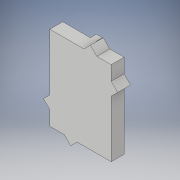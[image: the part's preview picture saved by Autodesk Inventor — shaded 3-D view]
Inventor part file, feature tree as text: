
AUTODESK INVENTOR PART (.ipt)
format: ipt  version: 2019 (Build 230136000, 136)  size: 216,576 bytes
history: native  units: mm
features: extrude x9, sketch x8
ambient origin geometry x8: Origin, YZ Plane, XZ Plane, XY Plane, X Axis, Y Axis, Z Axis, Center Point
bodies: Volumenkörper1 (feature_tree)
feature tree (17):
  sketch  "Skizze1"  dims[d0=50.5mm d1=35.5mm]
  extrude  "Extrusion1"  Depth=35.5mm
  extrude  "Extrusion2"  Depth=2.5mm TaperAngle=0.0deg
  extrude  "Extrusion3"  Depth=6.0mm
  extrude  "Extrusion4"  Depth=6.0mm
  extrude  "Extrusion5"  Depth=6.0mm TaperAngle=0.0deg
  extrude  "Extrusion8"  Depth=7.0mm
  extrude  "Extrusion9"  Depth=3.3mm
  extrude  "Extrusion10"  Depth=2.5mm TaperAngle=0.0deg
  extrude  "Extrusion11"  Depth=4.0mm
  sketch  "Skizze2"  dims[d2=2.5mm d3=2.5mm d4=0.0mm]
  sketch  "Skizze3"  dims[d5=6.0mm d6=0.0mm d7=3.0mm]
  sketch  "Skizze4"  dims[d8=77.5mm d9=0.0mm d11=6.0mm]
  sketch  "Skizze7"  dims[d12=6.0mm d13=0.0mm d15=6.0mm d16=0.0mm]
  sketch  "Skizze8"  dims[d26=7.0mm d27=7.0mm]
  sketch  "Skizze9"  dims[d28=3.3mm d29=3.3mm]
  sketch  "Skizze10"  dims[d30=2.5mm d31=0.0mm d32=2.5mm d33=0.0mm d35=4.0mm d36=4.0mm d37=0.0mm d38=1.5mm d39=1.5mm d40=4.0mm d41=0.0mm]
